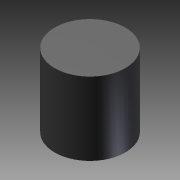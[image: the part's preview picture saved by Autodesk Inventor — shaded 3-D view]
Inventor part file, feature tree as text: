
AUTODESK INVENTOR PART (.ipt)
format: ipt  version: 2015 (Build 190159000, 159)  size: 87,040 bytes
history: native  units: in
note: dims shown in document units (in); Inventor stores cm internally (conversion verified against a paired STEP export)
features: other x14, revolve x1, sketch x1
ambient origin geometry x8: Origin, YZ Plane, XZ Plane, XY Plane, X Axis, Y Axis, Z Axis, Center Point
bodies: Solid1 (feature_tree)
feature tree (16):
  revolve  "Revolution1"  [1 undecoded]
  other  "to_bushing_XY"
  other  "to_bushing_YZ"
  other  "to_bushing_ZX"
  other  "to_bushing_X"
  other  "to_bushing_Y"
  other  "to_bushing_Z"
  other  "to_bushing_Center"
  other  "to_caps_S_XY"
  other  "to_caps_S_YZ"
  other  "to_caps_S_ZX"
  other  "to_caps_S_X"
  other  "to_caps_S_Y"
  other  "to_caps_S_Z"
  other  "to_caps_S_Center"
  sketch  "Sketch_1"  dims[d0=360.0deg]
note: 1 required parameter value undecoded (feature->parameter linkage not recoverable at this tier; creation-order binding heuristic only, values carry confidence <= 0.55)
